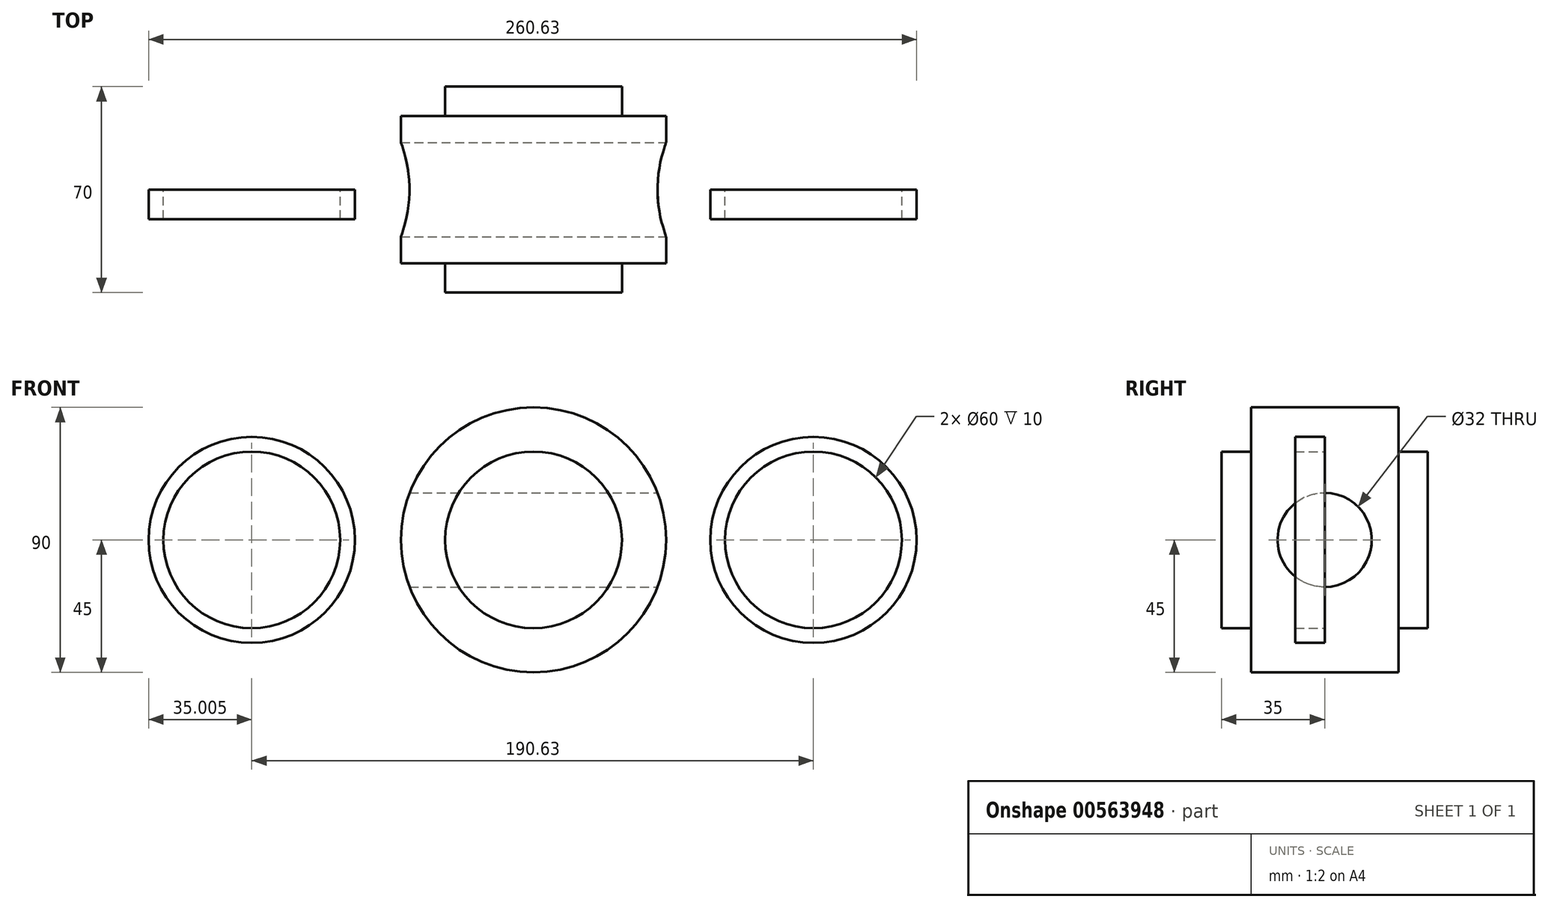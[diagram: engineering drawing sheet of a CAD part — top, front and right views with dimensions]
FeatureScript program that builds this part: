
annotation { "Feature Type Name" : "Feature", "Feature Type Description" : "" }
export const myFeature = defineFeature(function(context is Context, id is Id, definition is map)
    precondition{}
    {
        {
            var Q0;
            Q0=qCreatedBy(makeId("Front.planeOp"),FACE);
            var sketch = newSketch(context, id + "F0", { "sketchPlane" : qUnion([Q0])});
            skCircle(sketch, "E0", {"center": v(0, 0) * mm, "radius": 30 * mm});
            skCircle(sketch, "E1", {"center": v(0, 0) * mm, "radius": 45 * mm});
            skSolve(sketch);
        }
        {
            var Q0;
            Q0=makeQuery(id+"F0.imprint","IMPRINT",FACE,{"disambiguationData":[TD([[makeQuery(id+"F0.imprint","IMPRINT",EDGE,{"derivedFrom":sQuery(id+"F0.wireOp",EDGE,"E0")}),1.0]])]});
            extrude(context, id + "F1", {"entities" : qUnion([Q0]), "endBound" : BoundingType.SYMMETRIC, "depth" : 70 * mm, "offsetDistance" : 25 * mm});
        }
        {
            var Q0;
            Q0=qSketchRegion(id+"F0",true);
            extrude(context, id + "F2", {"entities" : qUnion([Q0]), "operationType" : NewBodyOperationType.ADD, "endBound" : BoundingType.SYMMETRIC, "depth" : 50 * mm, "offsetDistance" : 25 * mm});
        }
        {
            var Q0;
            Q0=qCreatedBy(makeId("Right.planeOp"),FACE);
            var sketch = newSketch(context, id + "F3", { "sketchPlane" : qUnion([Q0])});
            skCircle(sketch, "E2", {"center": v(0, 0) * mm, "radius": 16 * mm});
            skSolve(sketch);
        }
        {
            var Q0;
            Q0=qSketchRegion(id+"F3",true);
            extrude(context, id + "F4", {"entities" : qUnion([Q0]), "operationType" : NewBodyOperationType.REMOVE, "endBound" : BoundingType.SYMMETRIC, "oppositeDirection" : true, "depth" : 90 * mm, "offsetDistance" : 25 * mm});
        }
        {
            var Q0;
            Q0=qCreatedBy(makeId("Front.planeOp"),FACE);
            var sketch = newSketch(context, id + "F5", { "sketchPlane" : qUnion([Q0])});
            skCircle(sketch, "E3", {"center": v(95, 0) * mm, "radius": 30 * mm});
            skCircle(sketch, "E4", {"center": v(95, 0) * mm, "radius": 35 * mm});
            skCircle(sketch, "E5", {"center": v(-95.63, 0) * mm, "radius": 35 * mm});
            skCircle(sketch, "E6", {"center": v(-95.63, 0) * mm, "radius": 30 * mm});
            skSolve(sketch);
        }
        {
            var Q0;
            Q0=qSketchRegion(id+"F5",true);
            extrude(context, id + "F6", {"entities" : qUnion([Q0]), "depth" : 10 * mm, "offsetDistance" : 25 * mm});
        }
    });
